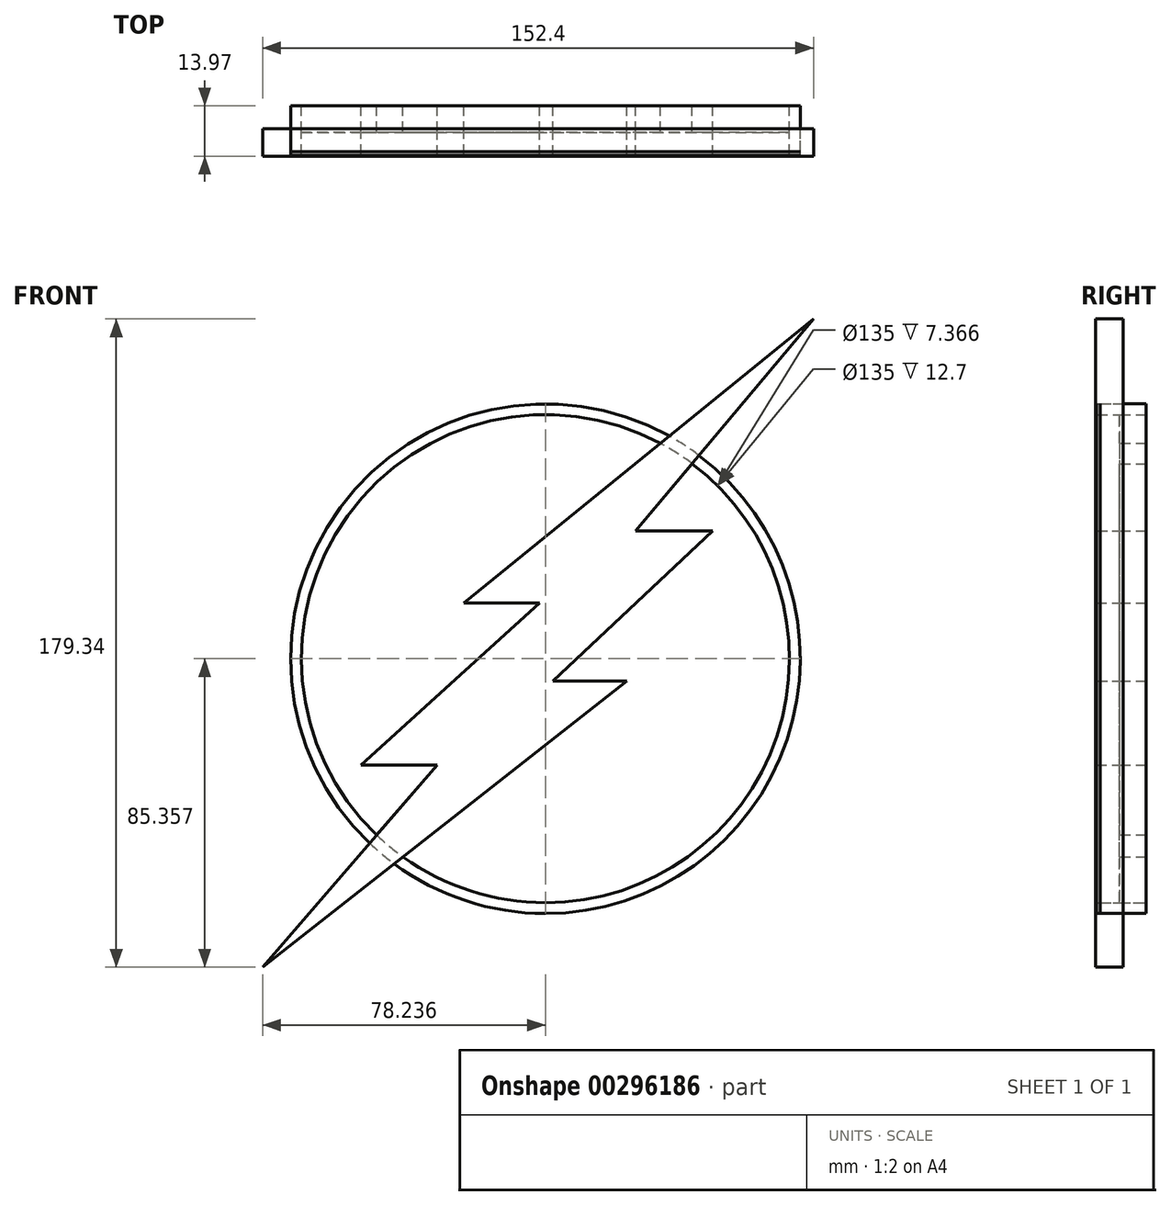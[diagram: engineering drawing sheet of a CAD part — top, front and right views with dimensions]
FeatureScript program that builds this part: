
annotation { "Feature Type Name" : "Feature", "Feature Type Description" : "" }
export const myFeature = defineFeature(function(context is Context, id is Id, definition is map)
    precondition{}
    {
        {
            var Q0;
            Q0=qCreatedBy(makeId("Front.planeOp"),FACE);
            var sketch = newSketch(context, id + "F0", { "sketchPlane" : qUnion([Q0])});
            skCircle(sketch, "E0", {"center": v(0.8, -1.24) * mm, "radius": 70.48 * mm});
            skCircle(sketch, "E1", {"center": v(0.8, -1.24) * mm, "radius": 67.5 * mm});
            skLineSegment(sketch, "E2", {"start": v(35.08, 60.34) * mm, "end": v(-21.72, 14.2) * mm});
            skLineSegment(sketch, "E3", {"start": v(-21.72, 14.2) * mm, "end": v(-0.85, 14.2) * mm});
            skLineSegment(sketch, "E4", {"start": v(-0.85, 14.2) * mm, "end": v(-50.17, -30.66) * mm});
            skLineSegment(sketch, "E5", {"start": v(-50.17, -30.66) * mm, "end": v(-29.1, -30.66) * mm});
            skLineSegment(sketch, "E6", {"start": v(-29.1, -30.66) * mm, "end": v(-77.44, -86.6) * mm});
            skLineSegment(sketch, "E7", {"start": v(-77.44, -86.6) * mm, "end": v(23.3, -7.37) * mm});
            skLineSegment(sketch, "E8", {"start": v(23.3, -7.37) * mm, "end": v(2.88, -7.37) * mm});
            skLineSegment(sketch, "E9", {"start": v(2.88, -7.37) * mm, "end": v(47.08, 34.09) * mm});
            skLineSegment(sketch, "E10", {"start": v(47.08, 34.09) * mm, "end": v(25.78, 34.09) * mm});
            skLineSegment(sketch, "E11", {"start": v(25.78, 34.09) * mm, "end": v(43.3, 54.98) * mm});
            skPoint(sketch, "E12", {"position": v(74.96, 92.74) * mm});
            skLineSegment(sketch, "E13", {"start": v(35.08, 60.34) * mm, "end": v(74.96, 92.74) * mm});
            skLineSegment(sketch, "E14", {"start": v(43.3, 54.98) * mm, "end": v(74.96, 92.74) * mm});
            skSolve(sketch);
        }
        {
            var Q0;
            {var subQ0=sQuery(id+"F0.wireOp",EDGE,"E2");var subQ5=sQuery(id+"F0.wireOp",EDGE,"E1");var subQ6=makeQuery(id+"F0.imprint","INTERSECT",VERTEX,{"derivedFrom":[subQ5,subQ0]});Q0=makeQuery(id+"F0.imprint","IMPRINT",FACE,{"disambiguationData":[TD([[makeQuery(id+"F0.imprint","IMPRINT",EDGE,{"disambiguationData":[TD([[subQ6,-1.0]])],"derivedFrom":subQ5}),-1.0]])]});}
            var Q1;
            {var subQ0=sQuery(id+"F0.wireOp",EDGE,"E11");var subQ5=sQuery(id+"F0.wireOp",EDGE,"E1");var subQ7=makeQuery(id+"F0.imprint","INTERSECT",VERTEX,{"derivedFrom":[subQ5,subQ0]});Q1=makeQuery(id+"F0.imprint","IMPRINT",FACE,{"disambiguationData":[TD([[makeQuery(id+"F0.imprint","IMPRINT",EDGE,{"disambiguationData":[TD([[subQ7,1.0]])],"derivedFrom":subQ5}),-1.0]])]});}
            var Q2;
            {var subQ0=sQuery(id+"F0.wireOp",EDGE,"E2");var subQ5=sQuery(id+"F0.wireOp",EDGE,"E1");var subQ7=makeQuery(id+"F0.imprint","INTERSECT",VERTEX,{"derivedFrom":[subQ5,subQ0]});Q2=makeQuery(id+"F0.imprint","IMPRINT",FACE,{"disambiguationData":[TD([[makeQuery(id+"F0.imprint","IMPRINT",EDGE,{"disambiguationData":[TD([[subQ7,1.0]])],"derivedFrom":subQ5}),-1.0]])]});}
            var Q3;
            {var subQ0=sQuery(id+"F0.wireOp",EDGE,"E6");var subQ1=sQuery(id+"F0.wireOp",EDGE,"E0");var subQ2=makeQuery(id+"F0.imprint","INTERSECT",VERTEX,{"derivedFrom":[subQ1,subQ0]});Q3=makeQuery(id+"F0.imprint","IMPRINT",FACE,{"disambiguationData":[TD([[makeQuery(id+"F0.imprint","IMPRINT",EDGE,{"disambiguationData":[TD([[subQ2,-1.0]])],"derivedFrom":subQ1}),1.0]])]});}
            extrude(context, id + "F1", {"entities" : qUnion([Q0, Q1, Q2, Q3]), "endBound" : BoundingType.SYMMETRIC, "depth" : 12.7 * mm});
        }
        {
            var Q0;
            {var subQ0=sQuery(id+"F0.wireOp",EDGE,"E6");var subQ1=sQuery(id+"F0.wireOp",EDGE,"E0");var subQ2=makeQuery(id+"F0.imprint","INTERSECT",VERTEX,{"derivedFrom":[subQ1,subQ0]});Q0=makeQuery(id+"F0.imprint","IMPRINT",FACE,{"disambiguationData":[TD([[makeQuery(id+"F0.imprint","IMPRINT",EDGE,{"disambiguationData":[TD([[subQ2,-1.0]])],"derivedFrom":subQ1}),-1.0]])]});}
            var Q1;
            {var subQ0=sQuery(id+"F0.wireOp",EDGE,"E6");var subQ1=sQuery(id+"F0.wireOp",EDGE,"E0");var subQ2=makeQuery(id+"F0.imprint","INTERSECT",VERTEX,{"derivedFrom":[subQ1,subQ0]});Q1=makeQuery(id+"F0.imprint","IMPRINT",FACE,{"disambiguationData":[TD([[makeQuery(id+"F0.imprint","IMPRINT",EDGE,{"disambiguationData":[TD([[subQ2,-1.0]])],"derivedFrom":subQ1}),1.0]])]});}
            var Q2;
            {var subQ12=sQuery(id+"F0.wireOp",EDGE,"E3");Q2=makeQuery(id+"F0.imprint","IMPRINT",FACE,{"disambiguationData":[TD([[makeQuery(id+"F0.imprint","IMPRINT",EDGE,{"derivedFrom":subQ12}),1.0]])]});}
            var Q3;
            {var subQ0=sQuery(id+"F0.wireOp",EDGE,"E13");Q3=makeQuery(id+"F0.imprint","IMPRINT",FACE,{"disambiguationData":[TD([[makeQuery(id+"F0.imprint","IMPRINT",EDGE,{"derivedFrom":subQ0}),-1.0]])]});}
            var Q4;
            {var subQ0=sQuery(id+"F0.wireOp",EDGE,"E2");var subQ5=sQuery(id+"F0.wireOp",EDGE,"E1");var subQ7=makeQuery(id+"F0.imprint","INTERSECT",VERTEX,{"derivedFrom":[subQ5,subQ0]});Q4=makeQuery(id+"F0.imprint","IMPRINT",FACE,{"disambiguationData":[TD([[makeQuery(id+"F0.imprint","IMPRINT",EDGE,{"disambiguationData":[TD([[subQ7,1.0]])],"derivedFrom":subQ5}),-1.0]])]});}
            extrude(context, id + "F2", {"entities" : qUnion([Q0, Q1, Q2, Q3, Q4]), "depth" : 7.62 * mm});
        }
        {
            var Q0;
            Q0=makeQuery(id+"F1.opExtrude","CAP_FACE",FACE,{"disambiguationData":[OSD([sQuery(id+"F0.wireOp",EDGE,"E0"),sQuery(id+"F0.wireOp",EDGE,"E1")])],"isStart":false});
            var Q1;
            {var subQ0=sQuery(id+"F0.wireOp",EDGE,"E3");Q1=makeQuery(id+"F0.imprint","IMPRINT",FACE,{"disambiguationData":[TD([[makeQuery(id+"F0.imprint","IMPRINT",EDGE,{"derivedFrom":subQ0}),-1.0]])]});}
            var Q2;
            {var subQ0=sQuery(id+"F0.wireOp",EDGE,"E8");Q2=makeQuery(id+"F0.imprint","IMPRINT",FACE,{"disambiguationData":[TD([[makeQuery(id+"F0.imprint","IMPRINT",EDGE,{"derivedFrom":subQ0}),-1.0]])]});}
            extrude(context, id + "F3", {"entities" : qUnion([Q0, Q1, Q2]), "depth" : 1.02 * mm, "hasSecondDirection" : true, "secondDirectionOppositeDirection" : true, "secondDirectionDepth" : 6.35 * mm});
        }
    });
